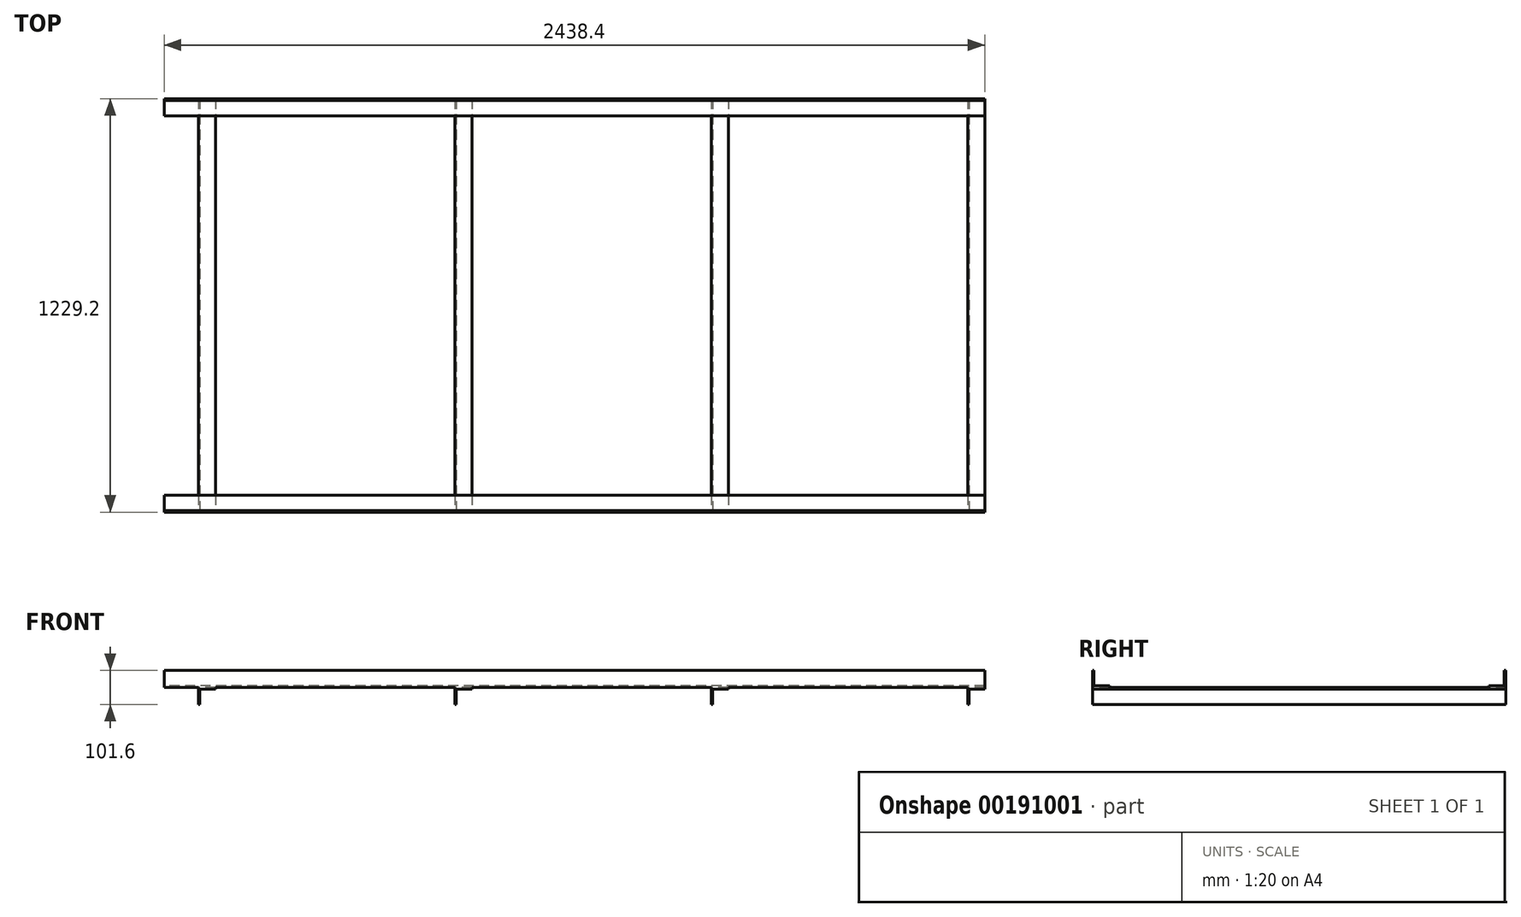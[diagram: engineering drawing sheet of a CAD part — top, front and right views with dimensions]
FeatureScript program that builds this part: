
annotation { "Feature Type Name" : "Feature", "Feature Type Description" : "" }
export const myFeature = defineFeature(function(context is Context, id is Id, definition is map)
    precondition{}
    {
        {
            var Q0;
            Q0=qCreatedBy(makeId("Right.planeOp"),FACE);
            var sketch = newSketch(context, id + "F0", { "sketchPlane" : qUnion([Q0])});
            skLineSegment(sketch, "E0", {"start": v(0, 0) * mm, "end": v(0, 50.8) * mm});
            skLineSegment(sketch, "E1", {"start": v(0, 0) * mm, "end": v(50.8, 0) * mm});
            skLineSegment(sketch, "E2.0", {"start": v(5, 5) * mm, "end": v(5, 50.8) * mm});
            skLineSegment(sketch, "E2.1", {"start": v(5, 5) * mm, "end": v(50.8, 5) * mm});
            skLineSegment(sketch, "E3", {"start": v(0, 50.8) * mm, "end": v(5, 50.8) * mm});
            skLineSegment(sketch, "E4", {"start": v(50.8, 5) * mm, "end": v(50.8, 0) * mm});
            skLineSegment(sketch, "E5", {"start": v(614.6, 119.65) * mm, "end": v(614.6, -143.95) * mm, "construction": true});
            skLineSegment(sketch, "E6.MirrorCS", {"start": v(1229.2, 50.8) * mm, "end": v(1224.2, 50.8) * mm});
            skLineSegment(sketch, "E7.MirrorCS", {"start": v(1178.4, 5) * mm, "end": v(1178.4, 0) * mm});
            skLineSegment(sketch, "E8.MirrorCS", {"start": v(1229.2, 0) * mm, "end": v(1229.2, 50.8) * mm});
            skLineSegment(sketch, "E9.MirrorCS", {"start": v(1229.2, 0) * mm, "end": v(1178.4, 0) * mm});
            skLineSegment(sketch, "E10.MirrorCS", {"start": v(1224.2, 5) * mm, "end": v(1178.4, 5) * mm});
            skLineSegment(sketch, "E11.MirrorCS", {"start": v(1224.2, 5) * mm, "end": v(1224.2, 50.8) * mm});
            skSolve(sketch);
        }
        {
            var Q0;
            Q0 = qSketchRegion(id + "F0", true);
            extrude(context, id + "F1", {"entities" : qUnion([Q0]), "depth" : 2438.4 * mm});
        }
        {
            var Q0;
            Q0=qCreatedBy(makeId("Front.planeOp"),FACE);
            var sketch = newSketch(context, id + "F2", { "sketchPlane" : qUnion([Q0])});
            skLineSegment(sketch, "E12", {"start": v(101.6, 306.58) * mm, "end": v(101.6, -597.37) * mm, "construction": true});
            skLineSegment(sketch, "E13.bottom", {"start": v(101.6, 0) * mm, "end": v(152.4, 0) * mm});
            skLineSegment(sketch, "E13.left", {"start": v(101.6, 0) * mm, "end": v(101.6, -50.8) * mm});
            skLineSegment(sketch, "E14.0", {"start": v(106.6, -5) * mm, "end": v(106.6, -50.8) * mm});
            skLineSegment(sketch, "E14.1", {"start": v(106.6, -5) * mm, "end": v(152.4, -5) * mm});
            skLineSegment(sketch, "E15", {"start": v(152.4, 0) * mm, "end": v(152.4, -5) * mm});
            skLineSegment(sketch, "E16", {"start": v(106.6, -50.8) * mm, "end": v(101.6, -50.8) * mm});
            skLineSegment(sketch, "E17.1.0.0", {"start": v(868.6, -5) * mm, "end": v(914.4, -5) * mm});
            skLineSegment(sketch, "E17.1.0.1", {"start": v(863.6, 306.58) * mm, "end": v(863.6, -597.37) * mm, "construction": true});
            skLineSegment(sketch, "E17.1.0.2", {"start": v(868.6, -5) * mm, "end": v(868.6, -50.8) * mm});
            skLineSegment(sketch, "E17.1.0.3", {"start": v(863.6, 0) * mm, "end": v(914.4, 0) * mm});
            skLineSegment(sketch, "E17.1.0.4", {"start": v(863.6, 0) * mm, "end": v(863.6, -50.8) * mm});
            skLineSegment(sketch, "E17.1.0.5", {"start": v(914.4, 0) * mm, "end": v(914.4, -5) * mm});
            skLineSegment(sketch, "E17.1.0.6", {"start": v(868.6, -50.8) * mm, "end": v(863.6, -50.8) * mm});
            skLineSegment(sketch, "E17.2.0.0", {"start": v(1630.6, -5) * mm, "end": v(1676.4, -5) * mm});
            skLineSegment(sketch, "E17.2.0.1", {"start": v(1625.6, 306.58) * mm, "end": v(1625.6, -597.37) * mm, "construction": true});
            skLineSegment(sketch, "E17.2.0.2", {"start": v(1630.6, -5) * mm, "end": v(1630.6, -50.8) * mm});
            skLineSegment(sketch, "E17.2.0.3", {"start": v(1625.6, 0) * mm, "end": v(1676.4, 0) * mm});
            skLineSegment(sketch, "E17.2.0.4", {"start": v(1625.6, 0) * mm, "end": v(1625.6, -50.8) * mm});
            skLineSegment(sketch, "E17.2.0.5", {"start": v(1676.4, 0) * mm, "end": v(1676.4, -5) * mm});
            skLineSegment(sketch, "E17.2.0.6", {"start": v(1630.6, -50.8) * mm, "end": v(1625.6, -50.8) * mm});
            skLineSegment(sketch, "E17.direction1", {"start": v(101.6, -597.37) * mm, "end": v(863.6, -597.37) * mm, "construction": true});
            skLineSegment(sketch, "E18.0.3.0", {"start": v(2392.6, -5) * mm, "end": v(2438.4, -5) * mm});
            skLineSegment(sketch, "E18.3.3.0", {"start": v(2387.6, 306.58) * mm, "end": v(2387.6, -597.37) * mm, "construction": true});
            skLineSegment(sketch, "E18.6.3.0", {"start": v(2392.6, -5) * mm, "end": v(2392.6, -50.8) * mm});
            skLineSegment(sketch, "E18.9.3.0", {"start": v(2387.6, 0) * mm, "end": v(2438.4, 0) * mm});
            skLineSegment(sketch, "E18.12.3.0", {"start": v(2387.6, 0) * mm, "end": v(2387.6, -50.8) * mm});
            skLineSegment(sketch, "E18.15.3.0", {"start": v(2438.4, 0) * mm, "end": v(2438.4, -5) * mm});
            skLineSegment(sketch, "E18.18.3.0", {"start": v(2392.6, -50.8) * mm, "end": v(2387.6, -50.8) * mm});
            skSolve(sketch);
        }
        {
            var Q0;
            Q0 = qSketchRegion(id + "F2", true);
            var Q1;
            Q1=makeQuery(id+"F1.opExtrude","SWEPT_FACE",FACE,{"disambiguationData":[OSD([sQuery(id+"F0.wireOp",EDGE,"E8.MirrorCS")])]});
            extrude(context, id + "F3", {"entities" : qUnion([Q0]), "operationType" : NewBodyOperationType.ADD, "endBound" : BoundingType.UP_TO_SURFACE, "oppositeDirection" : true, "endBoundEntityFace" : qUnion([Q1]), "depth" : 25.4 * mm});
        }
    });
